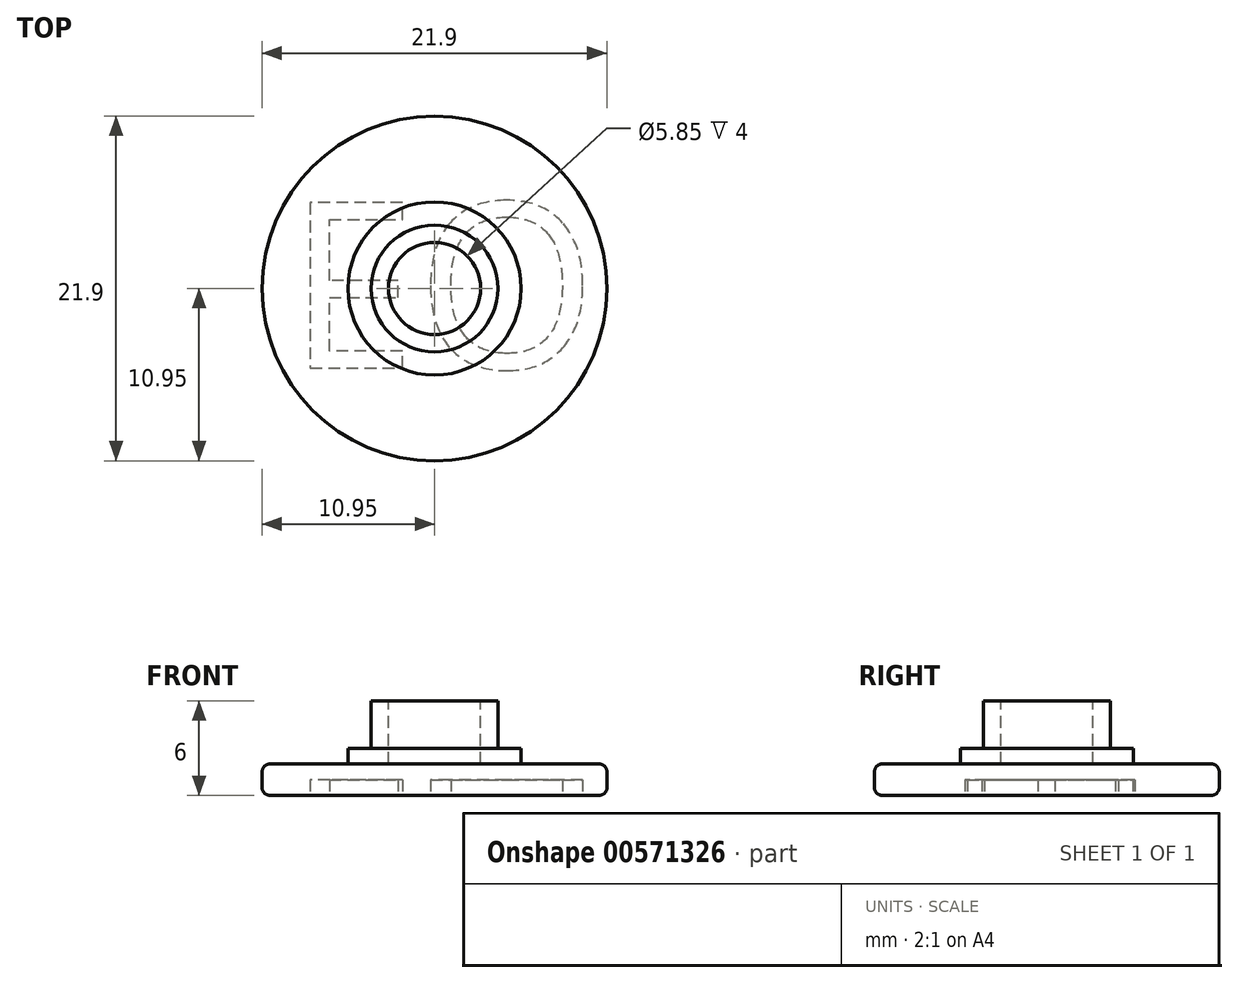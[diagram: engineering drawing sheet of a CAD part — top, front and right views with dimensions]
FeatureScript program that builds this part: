
annotation { "Feature Type Name" : "Feature", "Feature Type Description" : "" }
export const myFeature = defineFeature(function(context is Context, id is Id, definition is map)
    precondition{}
    {
        {
            var Q0;
            Q0=qCreatedBy(makeId("Top.planeOp"),FACE);
            var sketch = newSketch(context, id + "F0", { "sketchPlane" : qUnion([Q0])});
            skCircle(sketch, "E0", {"center": v(0, 0) * mm, "radius": 0.07 * mm});
            skCircle(sketch, "E1", {"center": v(0, 0) * mm, "radius": 10.95 * mm});
            skSolve(sketch);
        }
        {
            var Q0;
            Q0=qCreatedBy(makeId("Top.planeOp"),FACE);
            var sketch = newSketch(context, id + "F1", { "sketchPlane" : qUnion([Q0])});
            skCircle(sketch, "E2", {"center": v(0, 0) * mm, "radius": 5.5 * mm});
            skSolve(sketch);
        }
        {
            var Q0;
            Q0=qCreatedBy(makeId("Top.planeOp"),FACE);
            var sketch = newSketch(context, id + "F2", { "sketchPlane" : qUnion([Q0])});
            skCircle(sketch, "E3", {"center": v(0, 0) * mm, "radius": 4.03 * mm});
            skSolve(sketch);
        }
        {
            var Q0;
            Q0=qSketchRegion(id+"F0",true);
            extrude(context, id + "F3", {"entities" : qUnion([Q0]), "depth" : 2 * mm, "offsetDistance" : 25 * mm});
        }
        {
            var Q0;
            Q0=qSketchRegion(id+"F1",true);
            extrude(context, id + "F4", {"entities" : qUnion([Q0]), "operationType" : NewBodyOperationType.ADD, "depth" : 3 * mm});
        }
        {
            var Q0;
            Q0=qSketchRegion(id+"F2",true);
            extrude(context, id + "F5", {"entities" : qUnion([Q0]), "operationType" : NewBodyOperationType.ADD, "depth" : 6 * mm});
        }
        {
            var Q0;
            Q0=makeQuery(id+"F3.opExtrude","SWEPT_FACE",FACE,{"disambiguationData":[OSD([sQuery(id+"F0.wireOp",EDGE,"E1")])]});
            fillet(context, id + "F6", {"entities" : qUnion([Q0]), "radius" : .5 * mm, "tangentPropagation" : true, "allowEdgeOverflow" : false});
        }
        {
            var Q0;
            Q0=makeQuery(id+"F5.opExtrude","CAP_FACE",FACE,{"disambiguationData":[OSD([sQuery(id+"F2.wireOp",EDGE,"E3")])],"isStart":false});
            var sketch = newSketch(context, id + "F7", { "sketchPlane" : qUnion([Q0])});
            skCircle(sketch, "E4.0", {"center": v(0, 0) * mm, "radius": 2.92 * mm});
            skSolve(sketch);
        }
        {
            var Q0;
            Q0=qSketchRegion(id+"F7",true);
            extrude(context, id + "F8", {"entities" : qUnion([Q0]), "operationType" : NewBodyOperationType.REMOVE, "oppositeDirection" : true, "depth" : 4 * mm});
        }
        {
            var Q0;
            Q0=makeQuery(id+"F4.boolean.opBoolean","MERGE",FACE,{"derivedFrom":[makeQuery(id+"F3.opExtrude","CAP_FACE",FACE,{"disambiguationData":[OSD([sQuery(id+"F0.wireOp",EDGE,"E0"),sQuery(id+"F0.wireOp",EDGE,"E1")])],"isStart":true}),makeQuery(id+"F4.opExtrude","CAP_FACE",FACE,{"disambiguationData":[OSD([sQuery(id+"F1.wireOp",EDGE,"E2")])],"isStart":true})]});
            var sketch = newSketch(context, id + "F9", { "sketchPlane" : qUnion([Q0])});
            skSolve(sketch);
        }
        {
            var Q0;
            {var subQ0=sQuery(id+"F0.wireOp",EDGE,"E1");Q0=makeQuery(id+"F9.imprint","IMPRINT",FACE,{"disambiguationData":[TD([[makeQuery(id+"F9.imprint","IMPRINT",EDGE,{"derivedFrom":makeQuery(id+"F6.opFillet","BLEND_EDGE",EDGE,{"blendedFrom":[makeQuery(id+"F3.opExtrude","CAP_EDGE",EDGE,{"disambiguationData":[OSD([subQ0])],"isStart":true}),makeQuery(id+"F4.boolean.opBoolean","MERGE",FACE,{"derivedFrom":[makeQuery(id+"F3.opExtrude","CAP_FACE",FACE,{"disambiguationData":[OSD([sQuery(id+"F0.wireOp",EDGE,"E0"),subQ0])],"isStart":true}),makeQuery(id+"F4.opExtrude","CAP_FACE",FACE,{"disambiguationData":[OSD([sQuery(id+"F1.wireOp",EDGE,"E2")])],"isStart":true})]})],"blendedInto":[makeQuery(id+"F4.boolean.opBoolean","MERGE",FACE,{"derivedFrom":[makeQuery(id+"F3.opExtrude","CAP_FACE",FACE,{"disambiguationData":[OSD([sQuery(id+"F0.wireOp",EDGE,"E0"),subQ0])],"isStart":true}),makeQuery(id+"F4.opExtrude","CAP_FACE",FACE,{"disambiguationData":[OSD([sQuery(id+"F1.wireOp",EDGE,"E2")])],"isStart":true})]})]})}),1.0]])]});}
            var sketch = newSketch(context, id + "F10", { "sketchPlane" : qUnion([Q0])});
            skText(sketch, "E5", { "text": "EO\n", "fontName": "OpenSans-Regular.ttf"});
            const initialGuessF10  = {"E5": [-0.00934, -0.00546, 1, 0, 0.0106]};
            skSetInitialGuess(sketch, initialGuessF10);
            skSolve(sketch);
        }
        {
            var Q0;
            Q0 = qSketchRegion(id + "F10", true);
            extrude(context, id + "F11", {"entities" : qUnion([Q0]), "operationType" : NewBodyOperationType.REMOVE, "oppositeDirection" : true, "depth" : 1 * mm, "offsetDistance" : 25 * mm});
        }
    });
